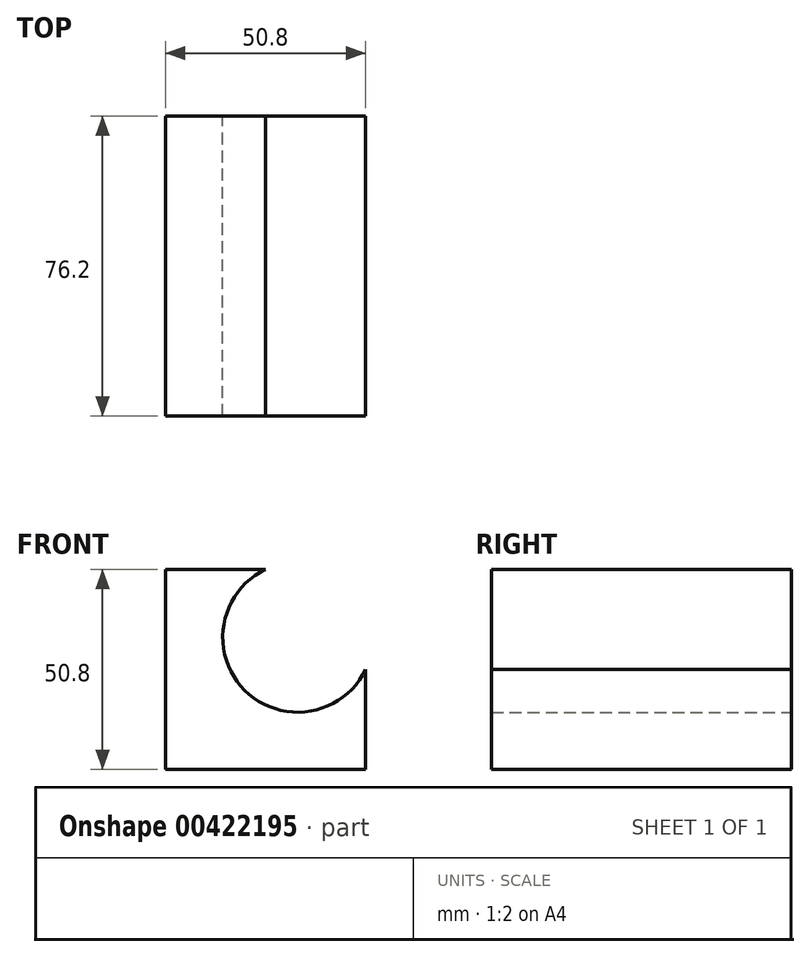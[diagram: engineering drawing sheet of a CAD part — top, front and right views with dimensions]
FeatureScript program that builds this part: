
annotation { "Feature Type Name" : "Feature", "Feature Type Description" : "" }
export const myFeature = defineFeature(function(context is Context, id is Id, definition is map)
    precondition{}
    {
        {
            var Q0;
            Q0=qCreatedBy(makeId("Front.planeOp"),FACE);
            var sketch = newSketch(context, id + "F0", { "sketchPlane" : qUnion([Q0])});
            skLineSegment(sketch, "E0.bottom", {"start": v(-13.94, 13.26) * mm, "end": v(11.46, 13.26) * mm});
            skLineSegment(sketch, "E0.top", {"start": v(-13.94, -37.54) * mm, "end": v(36.86, -37.54) * mm});
            skLineSegment(sketch, "E0.left", {"start": v(-13.94, 13.26) * mm, "end": v(-13.94, -37.54) * mm});
            skLineSegment(sketch, "E0.right", {"start": v(36.86, -12.14) * mm, "end": v(36.86, -37.54) * mm});
            skArc(sketch, "E1", {"start": v(11.46, 13.26) * mm, "mid": v(6.18, -17.43) * mm, "end": v(36.86, -12.14) * mm});
            skPoint(sketch, "E2.orphan", {"position": v(36.86, 13.26) * mm});
            skSolve(sketch);
        }
        {
            var Q0;
            Q0 = qSketchRegion(id + "F0", true);
            extrude(context, id + "F1", {"entities" : qUnion([Q0]), "depth" : 76.2 * mm});
        }
    });
